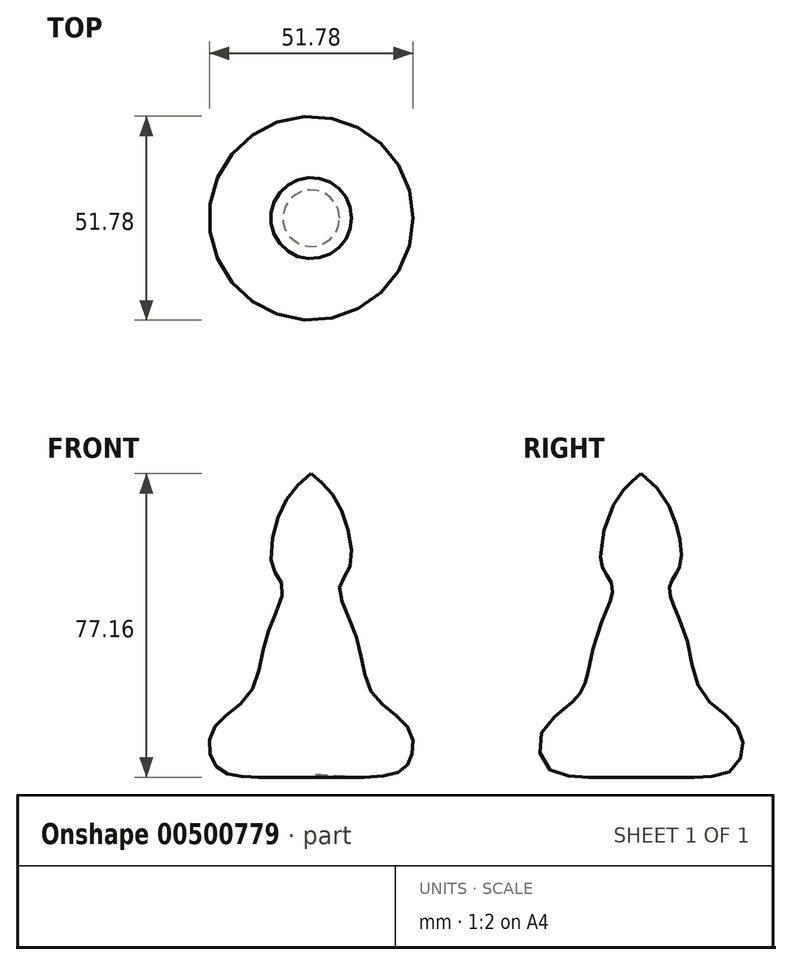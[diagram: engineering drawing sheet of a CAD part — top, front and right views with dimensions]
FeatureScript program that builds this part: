
annotation { "Feature Type Name" : "Feature", "Feature Type Description" : "" }
export const myFeature = defineFeature(function(context is Context, id is Id, definition is map)
    precondition{}
    {
        {
            var Q0;
            Q0=qCreatedBy(makeId("Front.planeOp"),FACE);
            var sketch = newSketch(context, id + "F0", { "sketchPlane" : qUnion([Q0])});
            skLineSegment(sketch, "E0", {"start": v(0, 0) * mm, "end": v(0, 76.4) * mm});
            skFitSpline(sketch, "E1", {"points": [v(0, 76.4) * mm, v(6.92, 68.58) * mm, v(9.93, 52.94) * mm, v(7.22, 47.52) * mm, v(11.43, 34.9) * mm, v(15.64, 20.45) * mm, v(24.66, 11.73) * mm, v(25.27, 3.91) * mm, v(20.75, 0) * mm, v(0, 0) * mm], "startDerivative": vector(70.05, -57.96) * mm, "endDerivative": vector(-163.72, 13.16) * mm});
            skSolve(sketch);
        }
        {
            var Q0;
            Q0=qSketchRegion(id+"F0",true);
            var Q1;
            Q1=sQuery(id+"F0.wireOp",EDGE,"E0");
            revolve(context, id + "F1", {"entities" : qUnion([Q0]), "axis" : qUnion([Q1]), "revolveType" : RevolveType.FULL});
        }
        {
            var Q0;
            Q0=makeQuery(id+"F1.opRevolve","SWEPT_BODY",BODY,{"disambiguationData":[OSD([sQuery(id+"F0.wireOp",EDGE,"E0"),sQuery(id+"F0.wireOp",EDGE,"E1")])]});
            transform(context, id + "F2", {"entities" : qUnion([Q0]), "transformType" : TransformType.TRANSLATION_3D, "dx" : 50.8 * mm, "dy" : 50.8 * mm, "dz" : 0 * mm, "makeCopy" : false});
        }
    });
